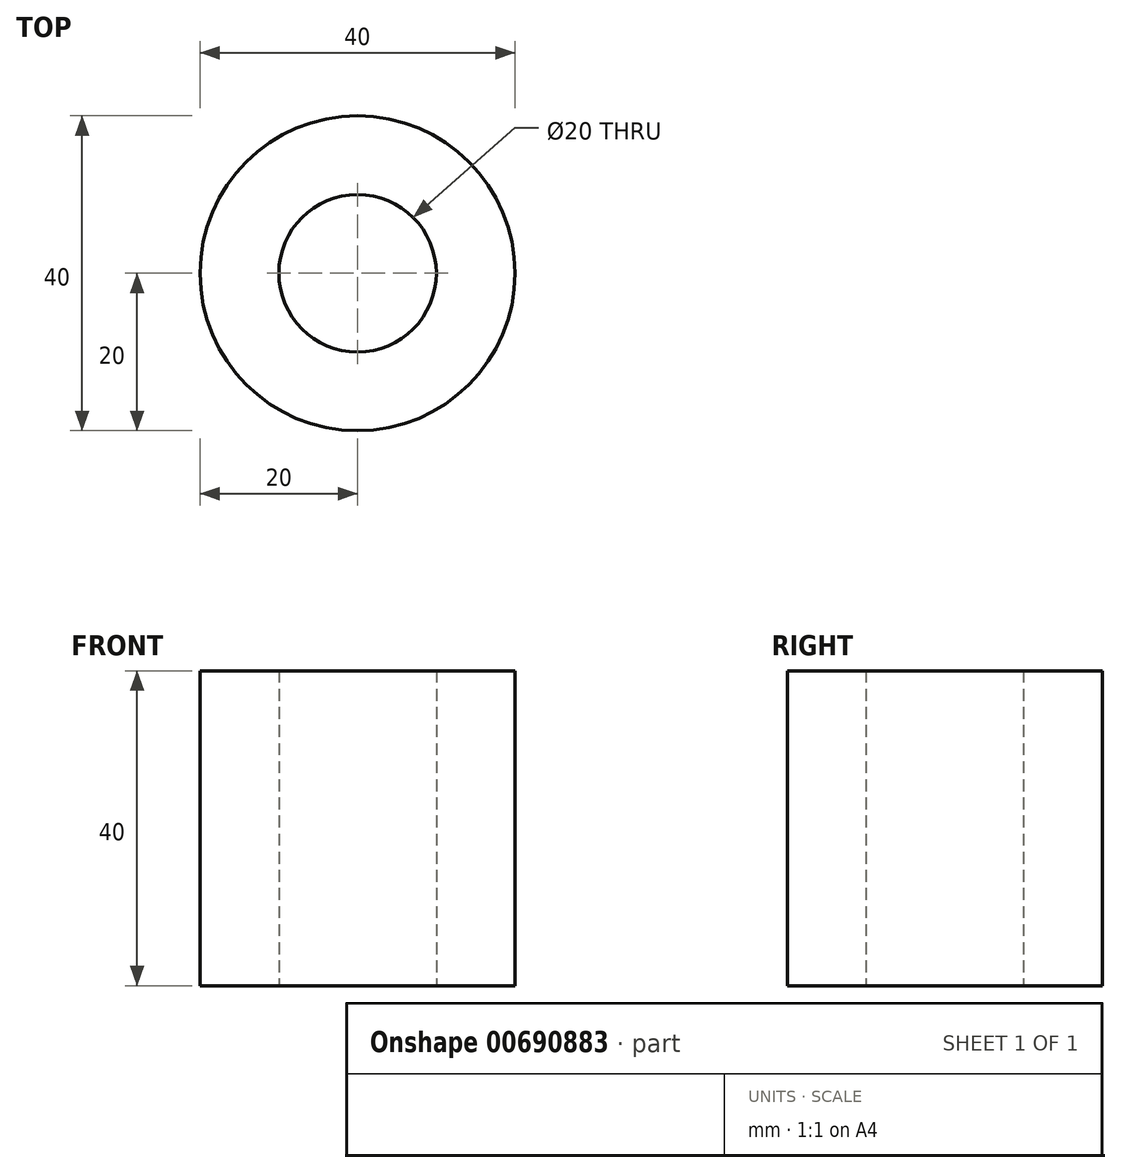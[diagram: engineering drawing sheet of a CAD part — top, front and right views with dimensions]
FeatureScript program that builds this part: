
annotation { "Feature Type Name" : "Feature", "Feature Type Description" : "" }
export const myFeature = defineFeature(function(context is Context, id is Id, definition is map)
    precondition{}
    {
        {
            var Q0;
            Q0=qCreatedBy(makeId("Top.planeOp"),FACE);
            var sketch = newSketch(context, id + "F0", { "sketchPlane" : qUnion([Q0])});
            skCircle(sketch, "E0", {"center": v(0, 0) * mm, "radius": 20 * mm});
            skCircle(sketch, "E1", {"center": v(0, 0) * mm, "radius": 10 * mm});
            skSolve(sketch);
        }
        {
            var Q0;
            Q0=makeQuery(id+"F0.imprint","IMPRINT",FACE,{"disambiguationData":[TD([[makeQuery(id+"F0.imprint","IMPRINT",EDGE,{"derivedFrom":sQuery(id+"F0.wireOp",EDGE,"E0")}),1.0]])]});
            extrude(context, id + "F1", {"entities" : qUnion([Q0]), "depth" : 40 * mm, "offsetDistance" : 25 * mm});
        }
    });
